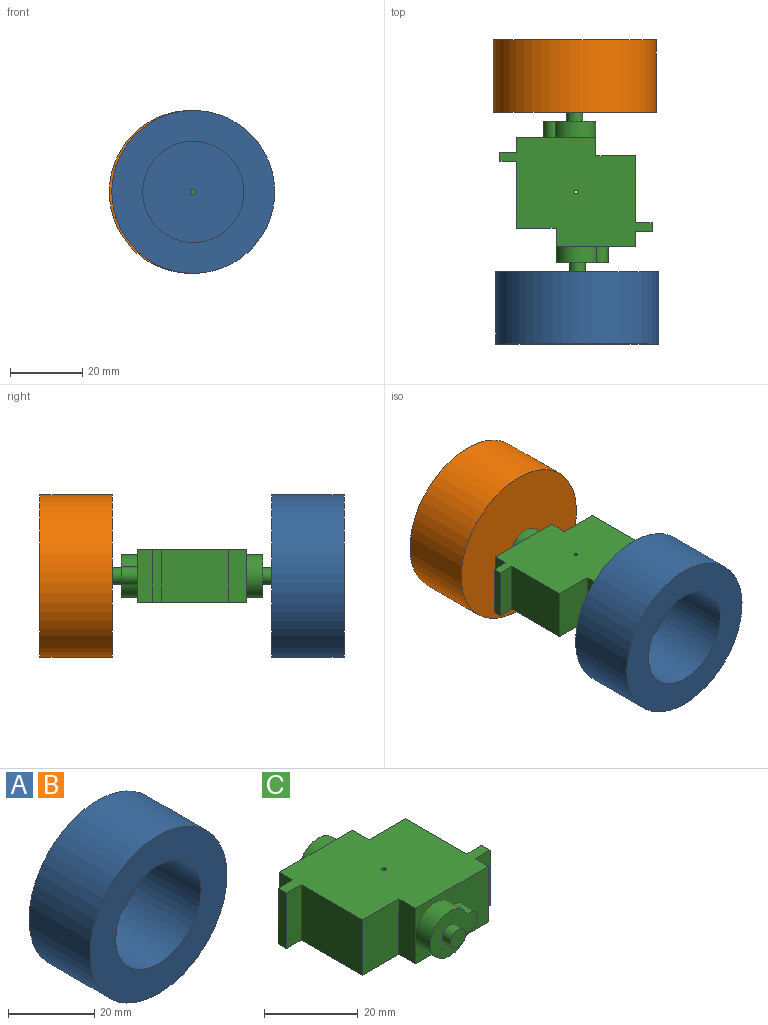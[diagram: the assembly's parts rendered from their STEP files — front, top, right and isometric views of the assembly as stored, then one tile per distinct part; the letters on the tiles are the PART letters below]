
ASSEMBLY  parts=3 mates=2
PART A: 6 faces, bbox 45x20x45 mm
  f0: plane 28x28mm, normal (0,-1,0), area 614mm2, adj f1,f5
  f1: cylinder r=14mm len=28mm, axis (0,1,0), area 1671.3mm2, adj f0,f3
  f2: cylinder r=22.5mm len=45mm, axis (0,1,0), area 2827.4mm2, adj f3,f4
  f3: plane 45x45mm, normal (0,-1,0), area 974.7mm2, adj f1,f2
  f4: plane 45x45mm, normal (0,1,0), area 1588.7mm2, adj f2,f5
  f5: cylinder r=0.75mm len=1.5mm, axis (0,-1,0), area 4.7mm2, adj f0,f4
PART B: same geometry as A
PART C: 29 faces, bbox 42x44x14.5 mm
  f0: plane 22x14.5mm, normal (0,-1,0), area 200mm2, adj f1,f15,f16,f17,f23,f24
  f1: plane 14.5x4mm, normal (1,0,0), area 58mm2, adj f0,f2,f16,f17
  f2: plane 14.5x4.5mm, normal (0,-1,0), area 65.2mm2, adj f1,f3,f16,f17
  f3: plane 14.5x2.5mm, normal (1,0,0), area 36.3mm2, adj f2,f4,f16,f17
  f4: plane 14.5x4.5mm, normal (0,1,0), area 65.2mm2, adj f3,f5,f16,f17
  f5: plane 18.5x14.5mm, normal (1,0,0), area 268.3mm2, adj f4,f6,f16,f17
  f6: plane 14.5x11mm, normal (0,1,0), area 159.5mm2, adj f5,f7,f16,f17
  f7: plane 14.5x5mm, normal (1,0,0), area 72.5mm2, adj f6,f8,f16,f17
  f8: plane 22x14.5mm, normal (0,1,0), area 200mm2, adj f7,f9,f16,f17,f18,f19
  f9: plane 14.5x4mm, normal (-1,0,0), area 58mm2, adj f8,f10,f16,f17
  f10: plane 14.5x4.5mm, normal (0,1,0), area 65.2mm2, adj f9,f11,f16,f17
  f11: plane 14.5x2.5mm, normal (-1,0,0), area 36.3mm2, adj f10,f12,f16,f17
  f12: plane 14.5x4.5mm, normal (0,-1,0), area 65.2mm2, adj f11,f13,f16,f17
  f13: plane 18.5x14.5mm, normal (-1,0,0), area 268.2mm2, adj f12,f14,f16,f17
  f14: plane 14.5x11mm, normal (0,-1,0), area 159.5mm2, adj f13,f15,f16,f17
  f15: plane 14.5x5mm, normal (-1,0,0), area 72.5mm2, adj f0,f14,f16,f17
  f16: plane 42x30mm, normal (0,0,1), area 901.7mm2, adj f0,f1,f2,f3,f4,f5,f6,f7
  f17: plane 42x30mm, normal (0,0,-1), area 901.7mm2, adj f0,f1,f2,f3,f4,f5,f6,f7
  f18: cylinder r=5.85mm len=11.7mm, axis (0,-1,0), area 143.1mm2, adj f8,f19,f20
  f19: cylinder r=2.5mm len=5mm, axis (0,-1,0), area 41.4mm2, adj f8,f18,f20
  f20: plane 14.35x11.7mm, normal (0,1,0), area 103mm2, adj f18,f19,f21
  f21: cylinder r=2.25mm len=4.5mm, axis (0,-1,0), area 35.3mm2, adj f20,f22
  f22: plane 4.5x4.5mm, normal (0,1,0), area 15.9mm2, adj f21
  f23: cylinder r=5.85mm len=11.7mm, axis (0,1,0), area 143.1mm2, adj f0,f24,f25
  f24: cylinder r=2.5mm len=5mm, axis (0,1,0), area 41.4mm2, adj f0,f23,f25
  f25: plane 14.35x11.7mm, normal (0,-1,0), area 103mm2, adj f23,f24,f26
  f26: cylinder r=2.25mm len=4.5mm, axis (0,1,0), area 35.3mm2, adj f25,f27
  f27: plane 4.5x4.5mm, normal (0,-1,0), area 15.9mm2, adj f26
  f28: cylinder r=0.5mm len=14.5mm, axis (0,0,1), area 45.6mm2, adj f16,f17
PLACE A t=(14.21,-29.14,8.43)mm
PLACE B rot(axis=(0,0,1),180deg) t=(13.51,14.86,8.43)mm
PLACE C t=(0.22,8.88,1.18)mm
MATE fastened A.f2 <-> C.f23  axis (0,1,0) through (14.21,-29.14,8.43)mm
MATE fastened B.f2 <-> C.f18  axis (0,-1,0) through (13.51,14.86,8.43)mm
